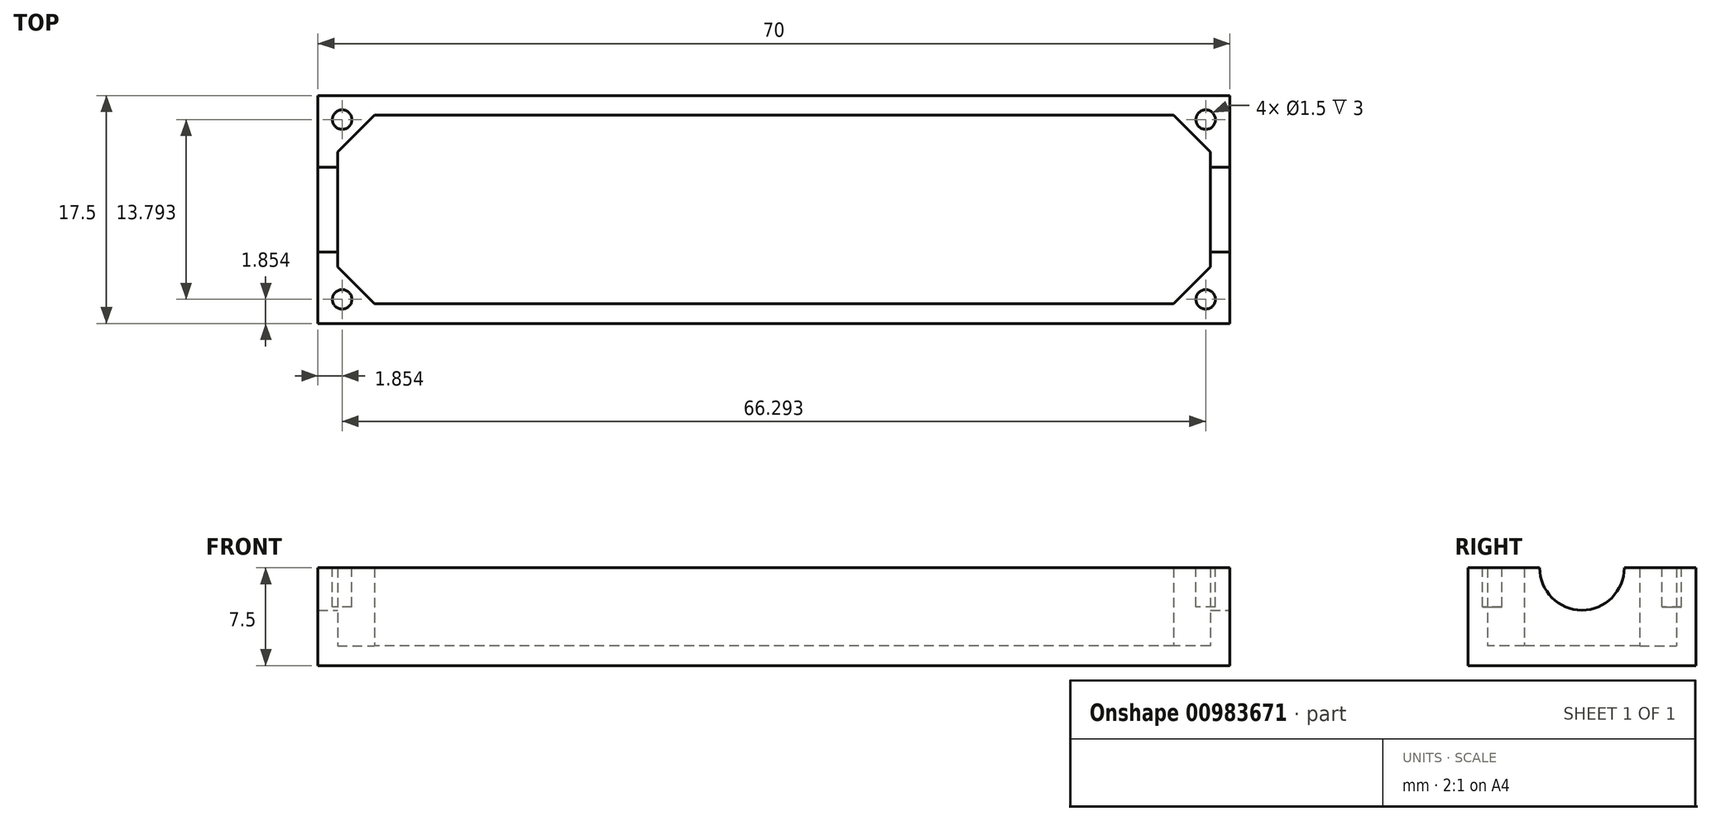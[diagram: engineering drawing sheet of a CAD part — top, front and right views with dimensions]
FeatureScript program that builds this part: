
annotation { "Feature Type Name" : "Feature", "Feature Type Description" : "" }
export const myFeature = defineFeature(function(context is Context, id is Id, definition is map)
    precondition{}
    {
        {
            var Q0;
            Q0=qCreatedBy(makeId("Top.planeOp"),FACE);
            var sketch = newSketch(context, id + "F0", { "sketchPlane" : qUnion([Q0])});
            skLineSegment(sketch, "E0.bottom", {"start": v(35, 8.75) * mm, "end": v(-35, 8.75) * mm});
            skLineSegment(sketch, "E0.top", {"start": v(35, -8.75) * mm, "end": v(-35, -8.75) * mm});
            skLineSegment(sketch, "E0.left", {"start": v(35, 8.75) * mm, "end": v(35, -8.75) * mm});
            skLineSegment(sketch, "E0.right", {"start": v(-35, 8.75) * mm, "end": v(-35, -8.75) * mm});
            skPoint(sketch, "E0.middle", {"position": v(0, 0) * mm});
            skSolve(sketch);
        }
        {
            var Q0;
            Q0 = qSketchRegion(id + "F0", true);
            extrude(context, id + "F1", {"entities" : qUnion([Q0]), "depth" : 7.5 * mm, "offsetDistance" : 25.4 * mm});
        }
        {
            var Q0;
            Q0=makeQuery(id+"F1.opExtrude","CAP_FACE",FACE,{"disambiguationData":[OSD([sQuery(id+"F0.wireOp",EDGE,"E0.bottom"),sQuery(id+"F0.wireOp",EDGE,"E0.top"),sQuery(id+"F0.wireOp",EDGE,"E0.left"),sQuery(id+"F0.wireOp",EDGE,"E0.right")])],"isStart":false});
            shell(context, id + "F2", {"entities" : qUnion([Q0]), "thickness" : 1.5 * mm});
        }
        {
            var Q0;
            Q0=makeQuery(id+"F2.opShell","OFFSET_FACE",FACE,{"disambiguationData":[OSD([sQuery(id+"F0.wireOp",EDGE,"E0.bottom"),sQuery(id+"F0.wireOp",EDGE,"E0.top"),sQuery(id+"F0.wireOp",EDGE,"E0.left"),sQuery(id+"F0.wireOp",EDGE,"E0.right")])]});
            var sketch = newSketch(context, id + "F3", { "sketchPlane" : qUnion([Q0])});
            skLineSegment(sketch, "E1", {"start": v(-33.5, 4.42) * mm, "end": v(-30.67, 7.25) * mm});
            skLineSegment(sketch, "E2", {"start": v(-30.67, 7.25) * mm, "end": v(-33.5, 7.25) * mm});
            skLineSegment(sketch, "E3", {"start": v(-33.5, 7.25) * mm, "end": v(-33.5, 4.42) * mm});
            skLineSegment(sketch, "E4", {"start": v(0, 0) * mm, "end": v(0, 7.25) * mm});
            skLineSegment(sketch, "E5.MirrorCS", {"start": v(33.5, 4.42) * mm, "end": v(30.67, 7.25) * mm});
            skLineSegment(sketch, "E6.MirrorCS", {"start": v(30.67, 7.25) * mm, "end": v(33.5, 7.25) * mm});
            skLineSegment(sketch, "E7.MirrorCS", {"start": v(33.5, 7.25) * mm, "end": v(33.5, 4.42) * mm});
            skLineSegment(sketch, "E8", {"start": v(0, 0) * mm, "end": v(33.5, 0) * mm});
            skLineSegment(sketch, "E9.MirrorCS", {"start": v(33.5, -4.42) * mm, "end": v(30.67, -7.25) * mm});
            skLineSegment(sketch, "E10.MirrorCS", {"start": v(30.67, -7.25) * mm, "end": v(33.5, -7.25) * mm});
            skLineSegment(sketch, "E11.MirrorCS", {"start": v(33.5, -7.25) * mm, "end": v(33.5, -4.42) * mm});
            skLineSegment(sketch, "E12.MirrorCS", {"start": v(-33.5, -7.25) * mm, "end": v(-33.5, -4.42) * mm});
            skLineSegment(sketch, "E13.MirrorCS", {"start": v(-30.67, -7.25) * mm, "end": v(-33.5, -7.25) * mm});
            skLineSegment(sketch, "E14.MirrorCS", {"start": v(-33.5, -4.42) * mm, "end": v(-30.67, -7.25) * mm});
            skSolve(sketch);
        }
        {
            var Q0;
            Q0 = qSketchRegion(id + "F3", true);
            var Q1;
            Q1=makeQuery(id+"F1.opExtrude","CAP_FACE",FACE,{"disambiguationData":[OSD([sQuery(id+"F0.wireOp",EDGE,"E0.bottom"),sQuery(id+"F0.wireOp",EDGE,"E0.top"),sQuery(id+"F0.wireOp",EDGE,"E0.left"),sQuery(id+"F0.wireOp",EDGE,"E0.right")])],"isStart":false});
            extrude(context, id + "F4", {"entities" : qUnion([Q0]), "operationType" : NewBodyOperationType.ADD, "endBound" : BoundingType.UP_TO_SURFACE, "depth" : 25 * mm, "endBoundEntityFace" : qUnion([Q1]), "offsetDistance" : 25 * mm});
        }
        {
            var Q0;
            Q0=makeQuery(id+"F4.boolean.opBoolean","MERGE",FACE,{"derivedFrom":[makeQuery(id+"F1.opExtrude","CAP_FACE",FACE,{"disambiguationData":[OSD([sQuery(id+"F0.wireOp",EDGE,"E0.bottom"),sQuery(id+"F0.wireOp",EDGE,"E0.top"),sQuery(id+"F0.wireOp",EDGE,"E0.left"),sQuery(id+"F0.wireOp",EDGE,"E0.right")])],"isStart":false}),makeQuery(id+"F4.opExtrude","CAP_FACE",FACE,{"disambiguationData":[OSD([sQuery(id+"F3.wireOp",EDGE,"E1"),sQuery(id+"F3.wireOp",EDGE,"E2"),sQuery(id+"F3.wireOp",EDGE,"E3")])],"isStart":false}),makeQuery(id+"F4.opExtrude","CAP_FACE",FACE,{"disambiguationData":[OSD([sQuery(id+"F3.wireOp",EDGE,"E7.MirrorCS"),sQuery(id+"F3.wireOp",EDGE,"E6.MirrorCS"),sQuery(id+"F3.wireOp",EDGE,"E5.MirrorCS")])],"isStart":false}),makeQuery(id+"F4.opExtrude","CAP_FACE",FACE,{"disambiguationData":[OSD([sQuery(id+"F3.wireOp",EDGE,"E9.MirrorCS"),sQuery(id+"F3.wireOp",EDGE,"E11.MirrorCS"),sQuery(id+"F3.wireOp",EDGE,"E10.MirrorCS")])],"isStart":false}),makeQuery(id+"F4.opExtrude","CAP_FACE",FACE,{"disambiguationData":[OSD([sQuery(id+"F3.wireOp",EDGE,"E12.MirrorCS"),sQuery(id+"F3.wireOp",EDGE,"E13.MirrorCS"),sQuery(id+"F3.wireOp",EDGE,"E14.MirrorCS")])],"isStart":false})]});
            var sketch = newSketch(context, id + "F5", { "sketchPlane" : qUnion([Q0])});
            skCircle(sketch, "E15", {"center": v(-33.15, 6.9) * mm, "radius": 0.75 * mm});
            skCircle(sketch, "E16", {"center": v(-33.15, -6.9) * mm, "radius": 0.75 * mm});
            skCircle(sketch, "E17", {"center": v(33.15, 6.9) * mm, "radius": 0.75 * mm});
            skCircle(sketch, "E18", {"center": v(33.15, -6.9) * mm, "radius": 0.75 * mm});
            skPoint(sketch, "E19.endSnap0", {"position": v(-32.09, 5.84) * mm});
            skLineSegment(sketch, "E20", {"start": v(-33.15, 6.9) * mm, "end": v(-32.09, 5.84) * mm});
            skLineSegment(sketch, "E21", {"start": v(-33.15, -6.9) * mm, "end": v(-32.09, -5.84) * mm});
            skLineSegment(sketch, "E22", {"start": v(33.15, -6.9) * mm, "end": v(32.09, -5.84) * mm});
            skLineSegment(sketch, "E23", {"start": v(33.15, 6.9) * mm, "end": v(32.09, 5.84) * mm});
            skSolve(sketch);
        }
        {
            var Q0;
            Q0 = qSketchRegion(id + "F5", true);
            extrude(context, id + "F6", {"entities" : qUnion([Q0]), "operationType" : NewBodyOperationType.REMOVE, "oppositeDirection" : true, "depth" : 3 * mm, "offsetDistance" : 25 * mm});
        }
        {
            var Q0;
            Q0=makeQuery(id+"F1.opExtrude","SWEPT_FACE",FACE,{"disambiguationData":[OSD([sQuery(id+"F0.wireOp",EDGE,"E0.left")])]});
            var sketch = newSketch(context, id + "F7", { "sketchPlane" : qUnion([Q0])});
            skCircle(sketch, "E24", {"center": v(0, 7.5) * mm, "radius": 3.25 * mm});
            skSolve(sketch);
        }
        {
            var Q0;
            Q0 = qSketchRegion(id + "F7", true);
            extrude(context, id + "F8", {"entities" : qUnion([Q0]), "operationType" : NewBodyOperationType.REMOVE, "endBound" : BoundingType.THROUGH_ALL, "oppositeDirection" : true, "depth" : 25 * mm, "offsetDistance" : 25 * mm});
        }
    });
